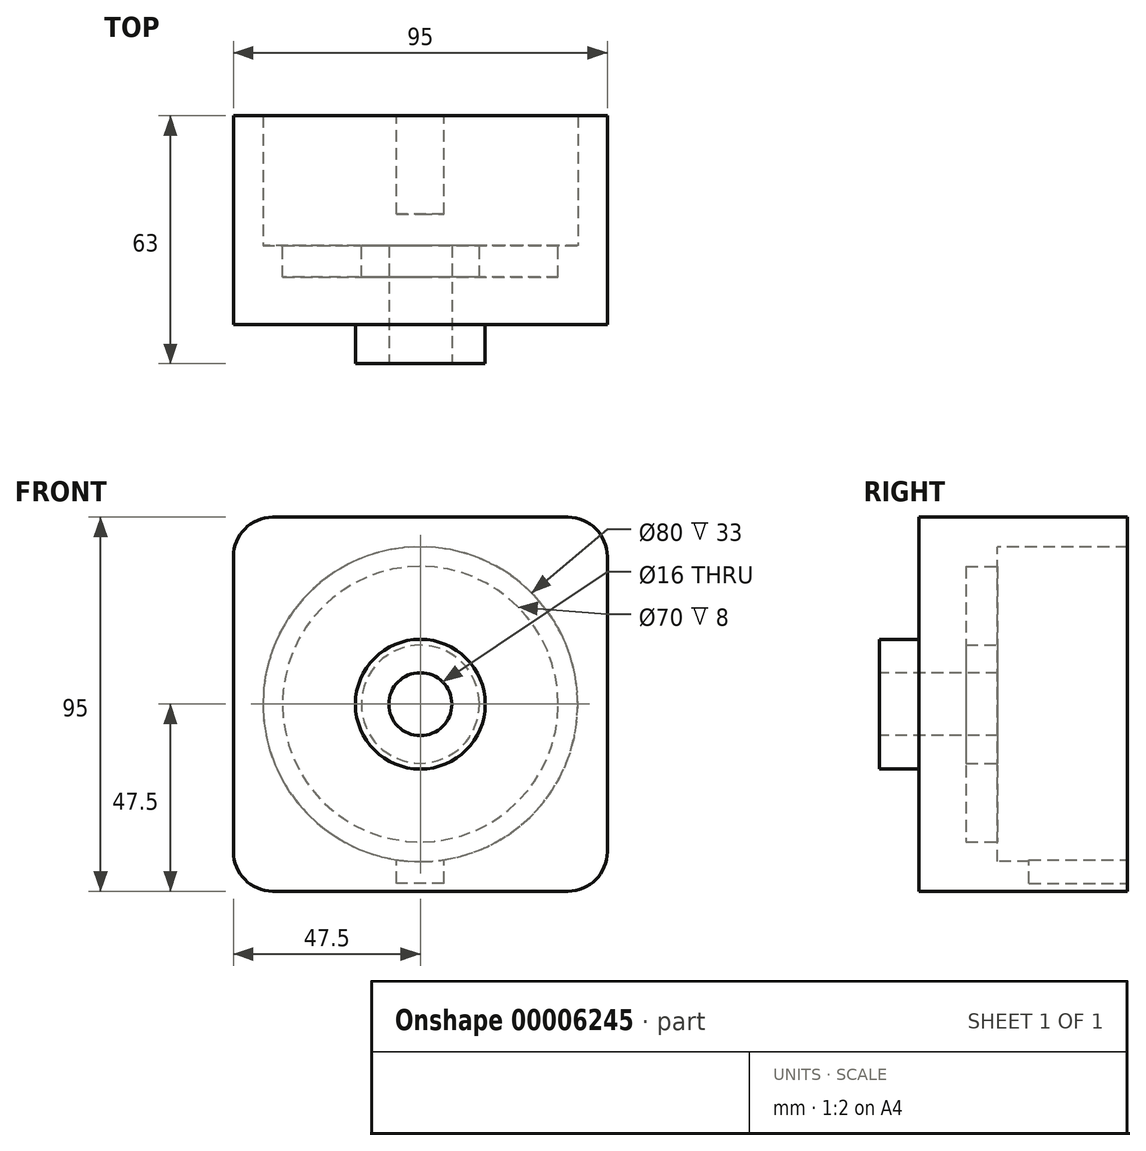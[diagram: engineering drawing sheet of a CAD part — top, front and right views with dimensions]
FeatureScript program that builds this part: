
annotation { "Feature Type Name" : "Feature", "Feature Type Description" : "" }
export const myFeature = defineFeature(function(context is Context, id is Id, definition is map)
    precondition{}
    {
        {
            var Q0;
            Q0=qCreatedBy(makeId("Right.planeOp"),FACE);
            var sketch = newSketch(context, id + "F0", { "sketchPlane" : qUnion([Q0])});
            skLineSegment(sketch, "E0.bottom", {"start": v(0, 8) * mm, "end": v(30, 8) * mm});
            skLineSegment(sketch, "E0.top", {"start": v(0, 40) * mm, "end": v(30, 40) * mm});
            skLineSegment(sketch, "E0.left", {"start": v(0, 8) * mm, "end": v(0, 40) * mm});
            skLineSegment(sketch, "E0.right", {"start": v(30, 8) * mm, "end": v(30, 40) * mm});
            skLineSegment(sketch, "E1", {"start": v(-29.5, 0) * mm, "end": v(55.83, 0) * mm, "construction": true});
            skSolve(sketch);
        }
        {
            var Q0;
            Q0=makeQuery(id+"F0.imprint","IMPRINT",FACE,{"disambiguationData":[TD([[makeQuery(id+"F0.imprint","IMPRINT",EDGE,{"derivedFrom":sQuery(id+"F0.wireOp",EDGE,"E0.bottom")}),1.0]])]});
            var Q1;
            Q1=sQuery(id+"F0.wireOp",EDGE,"E1");
            revolve(context, id + "F1", {"entities" : qUnion([Q0]), "axis" : qUnion([Q1]), "revolveType" : RevolveType.FULL});
        }
        {
            var Q0;
            Q0=makeQuery(id+"F1.opRevolve","SWEPT_FACE",FACE,{"disambiguationData":[OSD([sQuery(id+"F0.wireOp",EDGE,"E0.right")])]});
            var sketch = newSketch(context, id + "F2", { "sketchPlane" : qUnion([Q0])});
            skCircle(sketch, "E2", {"center": v(0, 0) * mm, "radius": 15 * mm});
            skCircle(sketch, "E3", {"center": v(0, 0) * mm, "radius": 35 * mm});
            skSolve(sketch);
        }
        {
            var Q0;
            Q0=makeQuery(id+"F2.imprint","IMPRINT",FACE,{"disambiguationData":[TD([[makeQuery(id+"F2.imprint","IMPRINT",EDGE,{"derivedFrom":sQuery(id+"F2.wireOp",EDGE,"E2")}),-1.0]])]});
            extrude(context, id + "F3", {"entities" : qUnion([Q0]), "operationType" : NewBodyOperationType.REMOVE, "oppositeDirection" : true, "depth" : 8 * mm});
        }
        {
            var Q0;
            Q0=makeQuery(id+"F1.opRevolve","SWEPT_FACE",FACE,{"disambiguationData":[OSD([sQuery(id+"F0.wireOp",EDGE,"E0.left")])]});
            var sketch = newSketch(context, id + "F4", { "sketchPlane" : qUnion([Q0])});
            skCircle(sketch, "E4", {"center": v(0, 0) * mm, "radius": 16.49 * mm});
            skCircle(sketch, "E5", {"center": v(0, 0) * mm, "radius": 53.9 * mm});
            skSolve(sketch);
        }
        {
            var Q0;
            Q0=makeQuery(id+"F4.imprint","IMPRINT",FACE,{"disambiguationData":[TD([[makeQuery(id+"F4.imprint","IMPRINT",EDGE,{"derivedFrom":sQuery(id+"F4.wireOp",EDGE,"E5")}),1.0]])]});
            var Q1;
            Q1=makeQuery(id+"F4.imprint","IMPRINT",FACE,{"disambiguationData":[TD([[makeQuery(id+"F4.imprint","IMPRINT",EDGE,{"derivedFrom":sQuery(id+"F4.wireOp",EDGE,"E4")}),-1.0]])]});
            extrude(context, id + "F5", {"entities" : qUnion([Q0, Q1]), "operationType" : NewBodyOperationType.REMOVE, "oppositeDirection" : true, "depth" : 10 * mm});
        }
        {
            var Q0;
            Q0=makeQuery(id+"F5.boolean.opBoolean","COPY",FACE,{"derivedFrom":makeQuery(id+"F5.opExtrude","CAP_FACE",FACE,{"disambiguationData":[OSD([sQuery(id+"F4.wireOp",EDGE,"E4"),sQuery(id+"F4.wireOp",EDGE,"E5")])],"isStart":false})});
            var sketch = newSketch(context, id + "F6", { "sketchPlane" : qUnion([Q0])});
            skPoint(sketch, "E6.rect.middle", {"position": v(0, 0) * mm});
            skPoint(sketch, "E6.rect.bottom.end.orphan", {"position": v(1.84, 6.05) * mm});
            skPoint(sketch, "E6.rect.bottom.start.orphan", {"position": v(-1.84, 6.05) * mm});
            skPoint(sketch, "E6.rect.top.end.orphan", {"position": v(1.84, -6.05) * mm});
            skPoint(sketch, "E6.rect.top.start.orphan", {"position": v(-1.84, -6.05) * mm});
            skLineSegment(sketch, "E7.rect.bottom", {"start": v(-37.5, 47.5) * mm, "end": v(37.5, 47.5) * mm});
            skLineSegment(sketch, "E7.rect.top", {"start": v(-37.5, -47.5) * mm, "end": v(37.5, -47.5) * mm});
            skLineSegment(sketch, "E7.rect.left", {"start": v(-47.5, 37.5) * mm, "end": v(-47.5, -37.5) * mm});
            skLineSegment(sketch, "E7.rect.right", {"start": v(47.5, 37.5) * mm, "end": v(47.5, -37.5) * mm});
            skPoint(sketch, "E8.visualSharp", {"position": v(-47.5, 47.5) * mm});
            skArc(sketch, "E8.filletArc", {"start": v(-37.5, 47.5) * mm, "mid": v(-44.57, 44.57) * mm, "end": v(-47.5, 37.5) * mm});
            skPoint(sketch, "E9.visualSharp", {"position": v(47.5, 47.5) * mm});
            skArc(sketch, "E9.filletArc", {"start": v(47.5, 37.5) * mm, "mid": v(44.57, 44.57) * mm, "end": v(37.5, 47.5) * mm});
            skPoint(sketch, "E10.visualSharp", {"position": v(47.5, -47.5) * mm});
            skArc(sketch, "E10.filletArc", {"start": v(37.5, -47.5) * mm, "mid": v(44.57, -44.57) * mm, "end": v(47.5, -37.5) * mm});
            skPoint(sketch, "E11.visualSharp", {"position": v(-47.5, -47.5) * mm});
            skArc(sketch, "E11.filletArc", {"start": v(-47.5, -37.5) * mm, "mid": v(-44.57, -44.57) * mm, "end": v(-37.5, -47.5) * mm});
            skSolve(sketch);
        }
        {
            var Q0;
            {var subQ5=sQuery(id+"F6.wireOp",EDGE,"E8.filletArc");Q0=makeQuery(id+"F6.imprint","IMPRINT",FACE,{"disambiguationData":[TD([[makeQuery(id+"F6.imprint","IMPRINT",EDGE,{"derivedFrom":subQ5}),1.0]])]});}
            var Q1;
            {var subQ5=sQuery(id+"F6.wireOp",EDGE,"E9.filletArc");Q1=makeQuery(id+"F6.imprint","IMPRINT",FACE,{"disambiguationData":[TD([[makeQuery(id+"F6.imprint","IMPRINT",EDGE,{"derivedFrom":subQ5}),1.0]])]});}
            var Q2;
            {var subQ5=sQuery(id+"F6.wireOp",EDGE,"E10.filletArc");Q2=makeQuery(id+"F6.imprint","IMPRINT",FACE,{"disambiguationData":[TD([[makeQuery(id+"F6.imprint","IMPRINT",EDGE,{"derivedFrom":subQ5}),1.0]])]});}
            var Q3;
            {var subQ5=sQuery(id+"F6.wireOp",EDGE,"E11.filletArc");Q3=makeQuery(id+"F6.imprint","IMPRINT",FACE,{"disambiguationData":[TD([[makeQuery(id+"F6.imprint","IMPRINT",EDGE,{"derivedFrom":subQ5}),1.0]])]});}
            var Q4;
            Q4=makeQuery(id+"F3.boolean.opBoolean","SPLIT",FACE,{"disambiguationData":[TD([makeQuery(id+"F1.opRevolve","SWEPT_FACE",FACE,{"disambiguationData":[OSD([sQuery(id+"F0.wireOp",EDGE,"E0.top")])]})])],"derivedFrom":makeQuery(id+"F1.opRevolve","SWEPT_FACE",FACE,{"disambiguationData":[OSD([sQuery(id+"F0.wireOp",EDGE,"E0.right")])]})});
            extrude(context, id + "F7", {"entities" : qUnion([Q0, Q1, Q2, Q3]), "operationType" : NewBodyOperationType.ADD, "oppositeDirection" : true, "endBoundEntity" : qUnion([Q4]), "depth" : (65 - 12) * mm});
        }
        {
            var Q0;
            Q0=makeQuery(id+"F7.opExtrude","CAP_FACE",FACE,{"disambiguationData":[OSD([sQuery(id+"F0.wireOp",EDGE,"E0.top"),sQuery(id+"F4.wireOp",EDGE,"E4"),sQuery(id+"F4.wireOp",EDGE,"E5"),sQuery(id+"F6.wireOp",EDGE,"E7.rect.bottom"),sQuery(id+"F6.wireOp",EDGE,"E7.rect.top"),sQuery(id+"F6.wireOp",EDGE,"E7.rect.left"),sQuery(id+"F6.wireOp",EDGE,"E7.rect.right"),sQuery(id+"F6.wireOp",EDGE,"E8.filletArc"),sQuery(id+"F6.wireOp",EDGE,"E9.filletArc"),sQuery(id+"F6.wireOp",EDGE,"E10.filletArc"),sQuery(id+"F6.wireOp",EDGE,"E11.filletArc")])],"isStart":false});
            var sketch = newSketch(context, id + "F8", { "sketchPlane" : qUnion([Q0])});
            skLineSegment(sketch, "E12.rect.bottom", {"start": v(-6, -45.5) * mm, "end": v(6, -45.5) * mm});
            skLineSegment(sketch, "E12.rect.top", {"start": v(-6, -33.82) * mm, "end": v(6, -33.82) * mm});
            skLineSegment(sketch, "E12.rect.left", {"start": v(-6, -45.5) * mm, "end": v(-6, -33.82) * mm});
            skLineSegment(sketch, "E12.rect.right", {"start": v(6, -45.5) * mm, "end": v(6, -33.82) * mm});
            skPoint(sketch, "E12.rect.middle", {"position": v(0, -39.66) * mm});
            skSolve(sketch);
        }
        {
            var Q0;
            {var subQ5=sQuery(id+"F8.wireOp",EDGE,"E12.rect.bottom");Q0=makeQuery(id+"F8.imprint","IMPRINT",FACE,{"disambiguationData":[TD([[makeQuery(id+"F8.imprint","IMPRINT",EDGE,{"derivedFrom":subQ5}),1.0]])]});}
            extrude(context, id + "F9", {"entities" : qUnion([Q0]), "operationType" : NewBodyOperationType.REMOVE, "oppositeDirection" : true, "depth" : 25 * mm});
        }
    });
